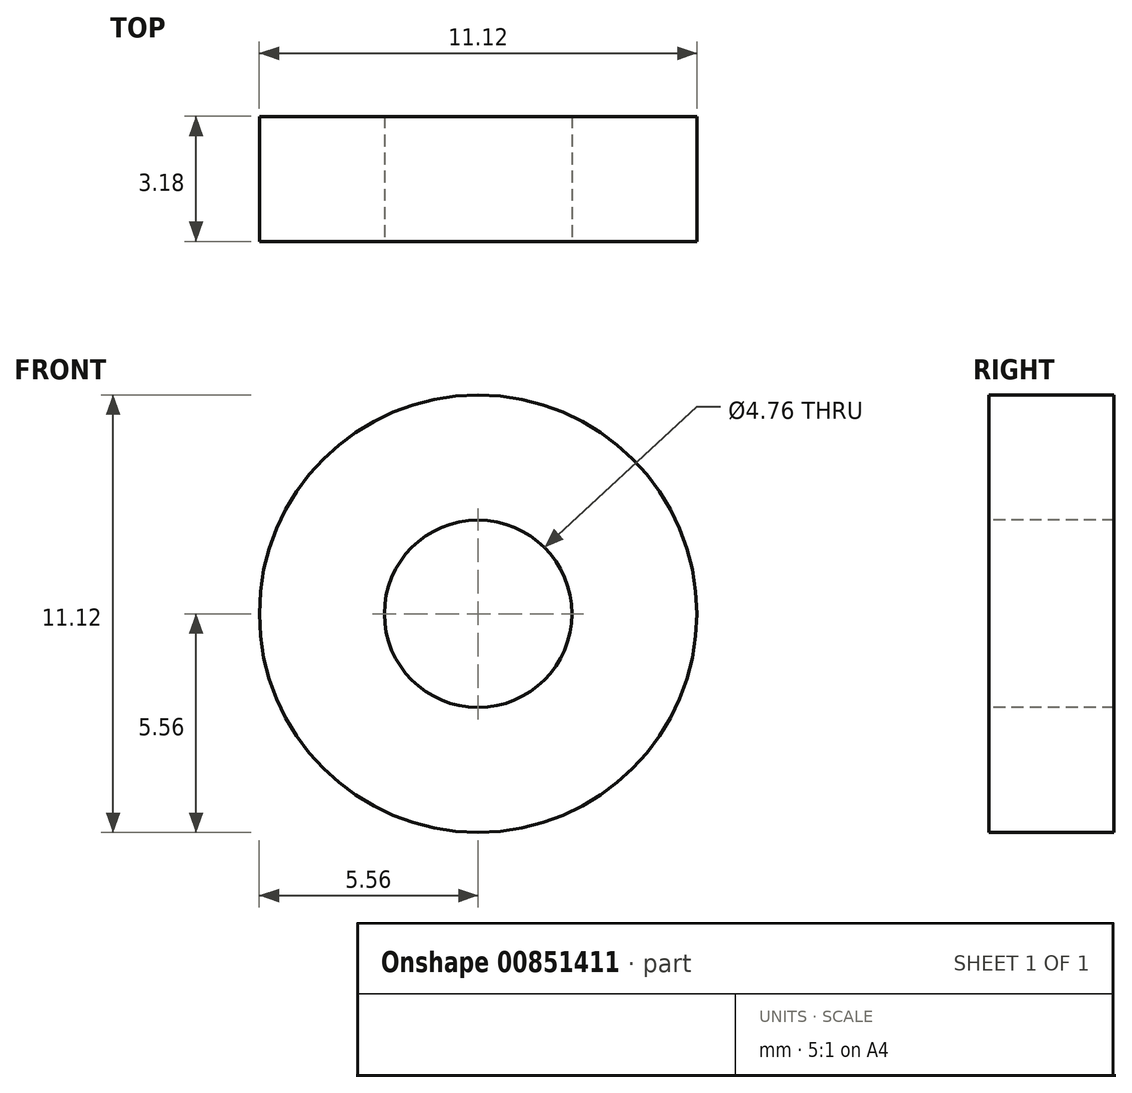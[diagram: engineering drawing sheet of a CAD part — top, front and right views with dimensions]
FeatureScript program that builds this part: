
annotation { "Feature Type Name" : "Feature", "Feature Type Description" : "" }
export const myFeature = defineFeature(function(context is Context, id is Id, definition is map)
    precondition{}
    {
        {
            var Q0;
            Q0=qCreatedBy(makeId("Front.planeOp"),FACE);
            var sketch = newSketch(context, id + "F0", { "sketchPlane" : qUnion([Q0])});
            skCircle(sketch, "E0", {"center": v(0, 0) * mm, "radius": 2.38 * mm});
            skCircle(sketch, "E1", {"center": v(0, 0) * mm, "radius": 5.56 * mm});
            skSolve(sketch);
        }
        {
            var Q0;
            Q0 = qSketchRegion(id + "F0", true);
            extrude(context, id + "F1", {"entities" : qUnion([Q0]), "oppositeDirection" : true, "depth" : 3.17 * mm, "offsetDistance" : 25.4 * mm});
        }
    });
